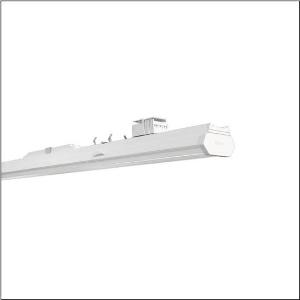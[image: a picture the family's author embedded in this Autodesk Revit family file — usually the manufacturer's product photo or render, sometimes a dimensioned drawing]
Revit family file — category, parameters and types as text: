
# Revit family: licross_11_protected_extreme_ho_51tp12dn4fxme
name_source: partatom
category: Lighting Fixtures
units: mm (PartAtom-declared; Revit-internal decimal feet)

## family parameters
Cut with Voids When Loaded = No
Host = Face
Light Source = No
Part Type = Normal
Room Calculation Point = No
Round Connector Dimension = Use Diameter
Shared = No

## types (1)
- --- (1 x LED, 15270 lm, 87.3 W, 4000K)
    Apparent Load = 87 VA
    CIE Flux Codes = 70 91 97 98 100
    Color Rendering = 80
    Color Temperature = 4000K
    Default Elevation = 1800 mm
    Description = Licross 11 Protected extreme HO, luminaire insert, of sheet steel, galvanised, coil coated, white, length: 1.500mm, width: 90mm, height: 101mm, LED rated luminous flux: 15.270lm, light colour: 840, SDCM (Standard Deviation of Colour Matching)MacAdam ≤ 2 SDCM (initial), control gear: DALI 2, with plug, 5-pole, with phase selection, mains connection: 220..240V, AC, 50/60Hz, rated input power: 87W, internal wiring halogen-free, primary optical cover: cover, of PMMA, light emission: direct distribution, primary light characteristic: symmetric, protection rating (complete): IP64, insulation class (complete): insulation class I (protective earthing), certification: CE, ENEC, VDE, UKCA, protection symbol: D if used in an environment with conductive dust loads with corresponding accessories, impact resistance: IK06, permissible ambient temperature for indoor applications: -40..+40°C, corresponds to IFS (International Featured Standards) requirements for safety and quality in the food industry, reducing of maximum allowable ambient temperature of 5°C with ceiling mounting, LABS conformity tested according to VDMA 24364:2018-05, The light source and the operating device comply with the requirements of the Ecodesign Regulation (EU) 2019/2020 and are replaceable in accordance with this regulation, packaging unit: 1 piece
    Height = 92 mm
    Lamp = 1 x LED
    Lamp Light Flux = 15270 lm
    Lamp Power = 87.3 W
    Lamp count = 1
    Length = 1500 mm
    Luminous efficacy = 175 lm/W
    Manufacturer = Siteco
    ModVariant = No
    Model = 51TP12DN4FXME
    Mounting Place = Ceiling
    Mounting Type = Pendant
    Number of Poles = 1
    OnlyDefault = Yes
    Power Factor = 1
    Product Name = Licross 11 Protected extreme HO
    Product group = luminaire insert | ceiling pendant
    ProductGroupID = 901
    Protection Class = Protection class I
    Protection Degree = IP 64
    RLX_Detail_Level = 1
    RLX_Emergency_Light_Flux = 0 lm
    RLX_Emergency_Type = 0
    RLX_Emergency_Type_DB = No
    RlxData = <blob elided: 24761 chars, md5=f4879599>
    Socket = socket
    Standby Power = 0 W
    System Light Flux = 15270 lm
    System Power = 87 W
    Type Comments = factory setting: luminous flux: 100 % | dim-lin: 254 | 589 mA
    Type Image = l_1256148.jpg
    URL = http://relux.com
    VarID = @adj_089301
    Voltage = 0 V
    Weight = 0.00 kg
    Width = 88 mm

## geometry (parser evidence)
native form markers: Blend x4, Sweep x9
no freeform markers — native parametric forms only
